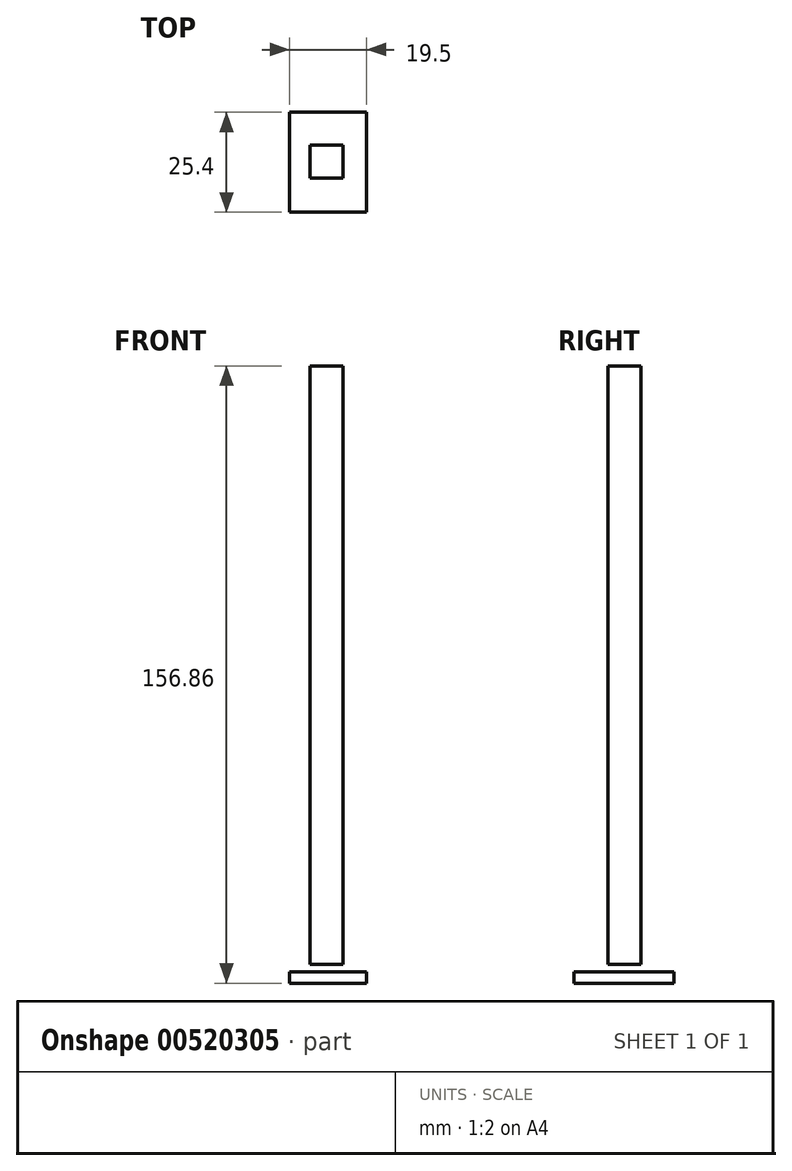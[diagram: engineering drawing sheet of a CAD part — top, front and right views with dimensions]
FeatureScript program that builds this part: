
annotation { "Feature Type Name" : "Feature", "Feature Type Description" : "" }
export const myFeature = defineFeature(function(context is Context, id is Id, definition is map)
    precondition{}
    {
        {
            var Q0;
            Q0=qCreatedBy(makeId("Front.planeOp"),FACE);
            var sketch = newSketch(context, id + "F0", { "sketchPlane" : qUnion([Q0])});
            skLineSegment(sketch, "E0.bottom", {"start": v(76.31, -76.05) * mm, "end": v(67.94, -76.05) * mm});
            skLineSegment(sketch, "E0.top", {"start": v(76.31, 76.04) * mm, "end": v(67.94, 76.04) * mm});
            skLineSegment(sketch, "E0.left", {"start": v(76.31, -76.05) * mm, "end": v(76.31, 76.04) * mm});
            skLineSegment(sketch, "E0.right", {"start": v(67.94, -76.05) * mm, "end": v(67.94, 76.04) * mm});
            skSolve(sketch);
        }
        {
            var Q0;
            Q0 = qSketchRegion(id + "F0", true);
            extrude(context, id + "F1", {"entities" : qUnion([Q0]), "depth" : 8.38 * mm, "offsetDistance" : 25.4 * mm});
        }
        {
            var Q0;
            Q0=qCreatedBy(makeId("Front.planeOp"),FACE);
            var sketch = newSketch(context, id + "F2", { "sketchPlane" : qUnion([Q0])});
            skLineSegment(sketch, "E1.bottom", {"start": v(82.22, -77.97) * mm, "end": v(62.72, -77.97) * mm});
            skLineSegment(sketch, "E1.top", {"start": v(82.22, -80.82) * mm, "end": v(62.72, -80.82) * mm});
            skLineSegment(sketch, "E1.left", {"start": v(82.22, -77.97) * mm, "end": v(82.22, -80.82) * mm});
            skLineSegment(sketch, "E1.right", {"start": v(62.72, -77.97) * mm, "end": v(62.72, -80.82) * mm});
            skSolve(sketch);
        }
        {
            var Q0;
            Q0 = qSketchRegion(id + "F2", true);
            extrude(context, id + "F3", {"entities" : qUnion([Q0]), "depth" : 25.4 * mm, "offsetDistance" : 25.4 * mm});
        }
        {
            var Q0;
            Q0=makeQuery(id+"F3.opExtrude","SWEPT_BODY",BODY,{"disambiguationData":[OSD([sQuery(id+"F2.wireOp",EDGE,"E1.bottom"),sQuery(id+"F2.wireOp",EDGE,"E1.top"),sQuery(id+"F2.wireOp",EDGE,"E1.left"),sQuery(id+"F2.wireOp",EDGE,"E1.right")])]});
            var Q1;
            Q1=makeQuery(id+"F3.opExtrude","CAP_FACE",FACE,{"disambiguationData":[OSD([sQuery(id+"F2.wireOp",EDGE,"E1.bottom"),sQuery(id+"F2.wireOp",EDGE,"E1.top"),sQuery(id+"F2.wireOp",EDGE,"E1.left"),sQuery(id+"F2.wireOp",EDGE,"E1.right")])],"isStart":true});
            transform(context, id + "F4", {"entities" : qUnion([Q0]), "transformType" : TransformType.TRANSLATION_DISTANCE, "transformDirection" : qUnion([Q1]), "distance" : 8.38 * mm, "makeCopy" : false});
        }
    });
